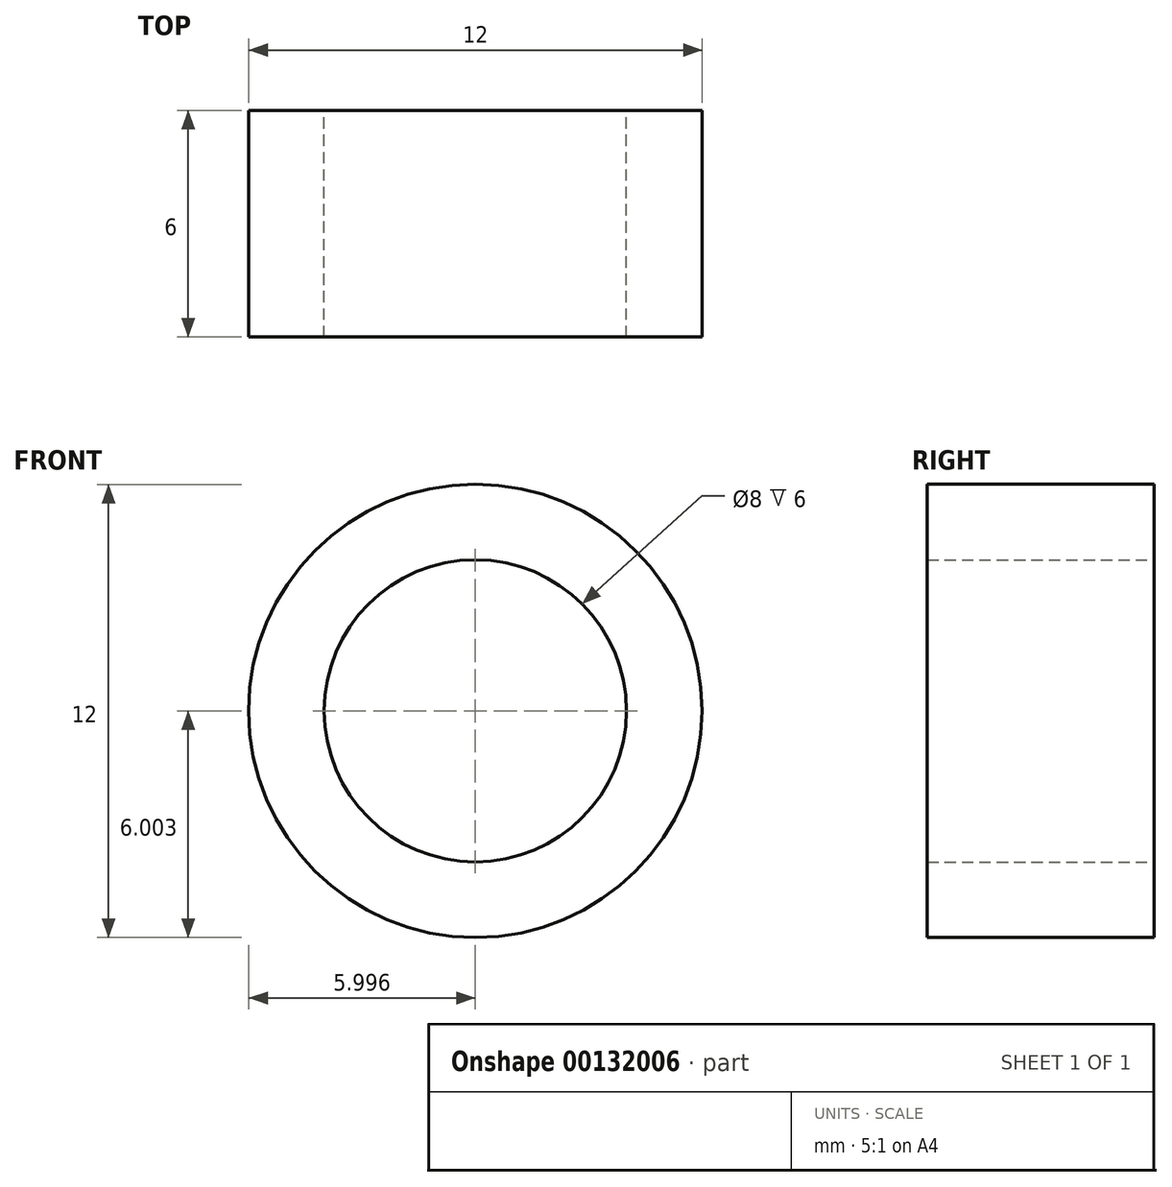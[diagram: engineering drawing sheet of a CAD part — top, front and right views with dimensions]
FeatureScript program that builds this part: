
annotation { "Feature Type Name" : "Feature", "Feature Type Description" : "" }
export const myFeature = defineFeature(function(context is Context, id is Id, definition is map)
    precondition{}
    {
        {
            var Q0;
            Q0=qCreatedBy(makeId("Front.planeOp"),FACE);
            var sketch = newSketch(context, id + "F0", { "sketchPlane" : qUnion([Q0])});
            skCircle(sketch, "E0", {"center": v(-30.87, 49.94) * mm, "radius": 4 * mm});
            skCircle(sketch, "E1", {"center": v(-30.87, 49.94) * mm, "radius": 6 * mm});
            skSolve(sketch);
        }
        {
            var Q0;
            Q0=makeQuery(id+"F0.imprint","IMPRINT",FACE,{"disambiguationData":[TD([[makeQuery(id+"F0.imprint","IMPRINT",EDGE,{"derivedFrom":sQuery(id+"F0.wireOp",EDGE,"E0")}),-1.0]])]});
            extrude(context, id + "F1", {"entities" : qUnion([Q0]), "depth" : 6 * mm});
        }
    });
